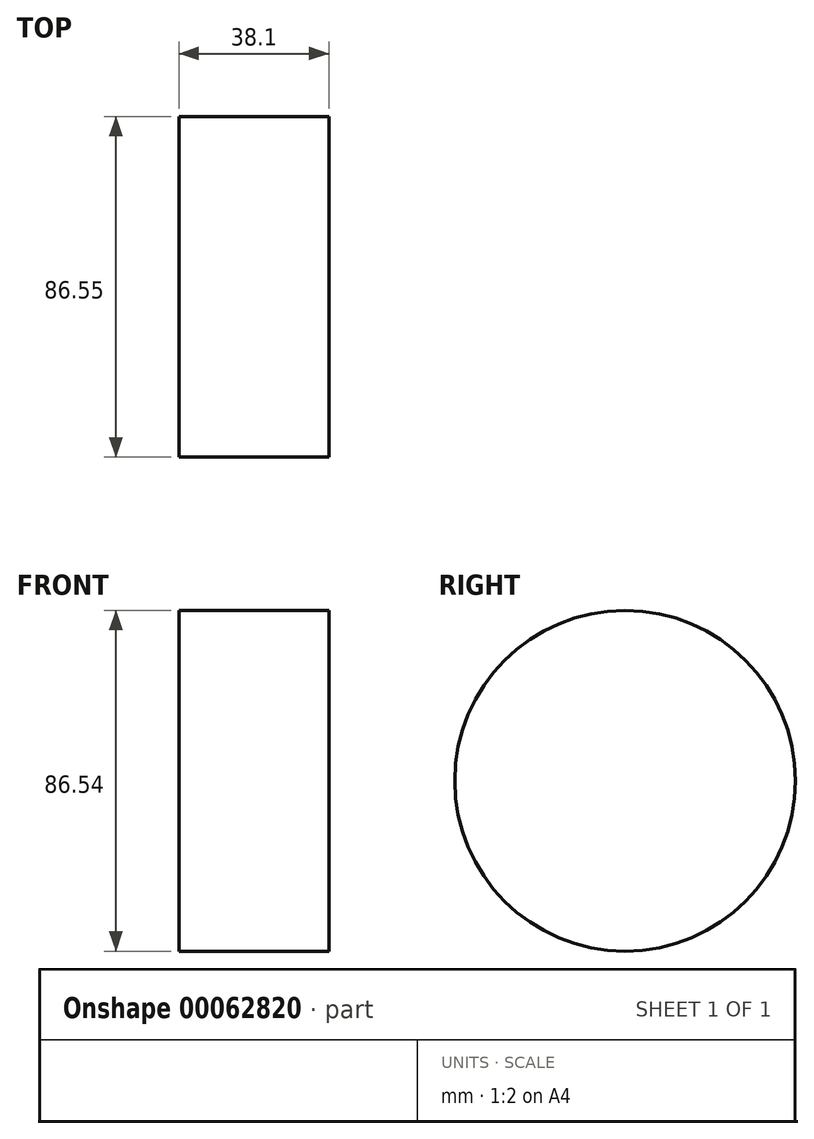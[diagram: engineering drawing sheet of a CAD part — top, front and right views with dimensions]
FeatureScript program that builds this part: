
annotation { "Feature Type Name" : "Feature", "Feature Type Description" : "" }
export const myFeature = defineFeature(function(context is Context, id is Id, definition is map)
    precondition{}
    {
        {
            var Q0;
            Q0=qCreatedBy(makeId("Right.planeOp"),FACE);
            var sketch = newSketch(context, id + "F0", { "sketchPlane" : qUnion([Q0])});
            skCircle(sketch, "E0", {"center": v(-19.91, 6.2) * mm, "radius": 43.27 * mm});
            skSolve(sketch);
        }
        {
            var Q0;
            Q0=makeQuery(id+"F0.imprint","IMPRINT",FACE,{"disambiguationData":[TD([[makeQuery(id+"F0.imprint","IMPRINT",EDGE,{"derivedFrom":sQuery(id+"F0.wireOp",EDGE,"E0")}),1.0]])]});
            extrude(context, id + "F1", {"entities" : qUnion([Q0]), "depth" : 38.1 * mm});
        }
    });
